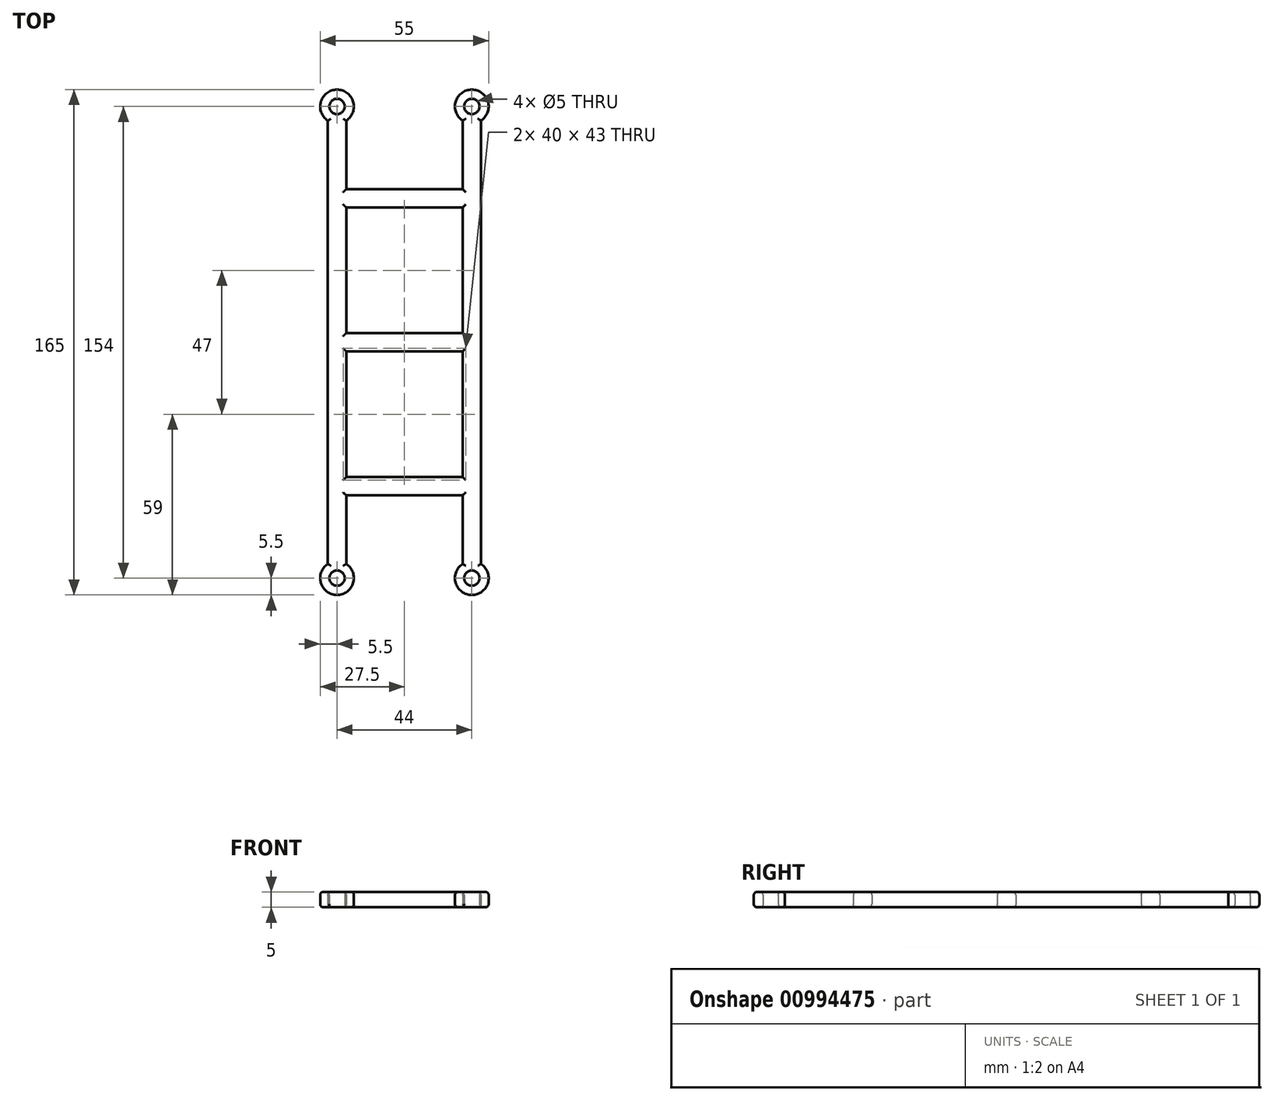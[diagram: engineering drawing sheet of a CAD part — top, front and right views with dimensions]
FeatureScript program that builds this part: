
annotation { "Feature Type Name" : "Feature", "Feature Type Description" : "" }
export const myFeature = defineFeature(function(context is Context, id is Id, definition is map)
    precondition{}
    {
        {
            assignVariable(context, id + "F0", {"name" : "winder_height", "anyValue" : 5});
        }
        {
            var Q0;
            Q0=qCreatedBy(makeId("Top.planeOp"),FACE);
            var sketch = newSketch(context, id + "F1", { "sketchPlane" : qUnion([Q0])});
            skPoint(sketch, "E0.middle", {"position": v(0, 0) * mm});
            skLineSegment(sketch, "E1.bottom", {"start": v(0, 0) * mm, "end": v(25, 0) * mm});
            skLineSegment(sketch, "E1.left", {"start": v(0, 0) * mm, "end": v(0, 50) * mm});
            skLineSegment(sketch, "E1.right", {"start": v(25, 0) * mm, "end": v(25, 50) * mm});
            skLineSegment(sketch, "E2.bottom", {"start": v(25, 50) * mm, "end": v(19, 50) * mm, "construction": true});
            skLineSegment(sketch, "E3", {"start": v(0, 50) * mm, "end": v(19, 50) * mm});
            skLineSegment(sketch, "E4", {"start": v(25, 50) * mm, "end": v(25, 80) * mm});
            skLineSegment(sketch, "E5", {"start": v(25, 80) * mm, "end": v(19, 80) * mm});
            skLineSegment(sketch, "E6", {"start": v(19, 80) * mm, "end": v(19, 50) * mm});
            skLineSegment(sketch, "E7", {"start": v(22, 50) * mm, "end": v(22, 77) * mm, "construction": true});
            skCircle(sketch, "E8", {"center": v(22, 77) * mm, "radius": 2.5 * mm});
            skLineSegment(sketch, "E9.bottom", {"start": v(0, 44) * mm, "end": v(19, 44) * mm});
            skLineSegment(sketch, "E9.top", {"start": v(0, 3) * mm, "end": v(19, 3) * mm});
            skLineSegment(sketch, "E9.left", {"start": v(0, 44) * mm, "end": v(0, 3) * mm});
            skLineSegment(sketch, "E9.right", {"start": v(19, 44) * mm, "end": v(19, 3) * mm});
            skCircle(sketch, "E10", {"center": v(22, 77) * mm, "radius": 5.5 * mm});
            skSolve(sketch);
        }
        {
            var Q0;
            {var subQ8=sQuery(id+"F1.wireOp",EDGE,"E1.bottom");Q0=makeQuery(id+"F1.imprint","IMPRINT",FACE,{"disambiguationData":[TD([[makeQuery(id+"F1.imprint","IMPRINT",EDGE,{"derivedFrom":subQ8}),1.0]])]});}
            var Q1;
            {var subQ0=sQuery(id+"F1.wireOp",EDGE,"E5");Q1=makeQuery(id+"F1.imprint","IMPRINT",FACE,{"disambiguationData":[TD([[makeQuery(id+"F1.imprint","IMPRINT",EDGE,{"derivedFrom":subQ0}),-1.0]])]});}
            var Q2;
            {var subQ1=sQuery(id+"F1.wireOp",EDGE,"E5");Q2=makeQuery(id+"F1.imprint","IMPRINT",FACE,{"disambiguationData":[TD([[makeQuery(id+"F1.imprint","IMPRINT",EDGE,{"derivedFrom":subQ1}),1.0]])]});}
            var Q3;
            Q3=sQuery(id+"F1.wireOp",EDGE,"E2.bottom");
            extrude(context, id + "F2", {"entities" : qUnion([Q0, Q1, Q2]), "surfaceEntities" : qUnion([Q3]), "depth" : (getVariable(context, 'winder_height')) * mm, "offsetDistance" : 25 * mm});
        }
        {
            var Q0;
            Q0=makeQuery(id+"F2.opExtrude","SWEPT_BODY",BODY,{"disambiguationData":[OSD([sQuery(id+"F1.wireOp",EDGE,"E1.bottom"),sQuery(id+"F1.wireOp",EDGE,"E1.left"),sQuery(id+"F1.wireOp",EDGE,"E1.right"),sQuery(id+"F1.wireOp",EDGE,"E3"),sQuery(id+"F1.wireOp",EDGE,"E4"),sQuery(id+"F1.wireOp",EDGE,"E6"),sQuery(id+"F1.wireOp",EDGE,"E8"),sQuery(id+"F1.wireOp",EDGE,"E9.bottom"),sQuery(id+"F1.wireOp",EDGE,"E9.top"),sQuery(id+"F1.wireOp",EDGE,"E9.right"),sQuery(id+"F1.wireOp",EDGE,"E10")])]});
            var Q1;
            Q1=qCreatedBy(makeId("Front.planeOp"),FACE);
            mirror(context, id + "F3", {"operationType" : NewBodyOperationType.ADD, "entities" : qUnion([Q0]), "mirrorPlane" : qUnion([Q1])});
        }
        {
            var Q0;
            Q0=makeQuery(id+"F2.opExtrude","SWEPT_BODY",BODY,{"disambiguationData":[OSD([sQuery(id+"F1.wireOp",EDGE,"E1.bottom"),sQuery(id+"F1.wireOp",EDGE,"E1.left"),sQuery(id+"F1.wireOp",EDGE,"E1.right"),sQuery(id+"F1.wireOp",EDGE,"E3"),sQuery(id+"F1.wireOp",EDGE,"E4"),sQuery(id+"F1.wireOp",EDGE,"E6"),sQuery(id+"F1.wireOp",EDGE,"E8"),sQuery(id+"F1.wireOp",EDGE,"E9.bottom"),sQuery(id+"F1.wireOp",EDGE,"E9.top"),sQuery(id+"F1.wireOp",EDGE,"E9.right"),sQuery(id+"F1.wireOp",EDGE,"E10")])]});
            var Q1;
            Q1=qCreatedBy(makeId("Right.planeOp"),FACE);
            mirror(context, id + "F4", {"operationType" : NewBodyOperationType.ADD, "entities" : qUnion([Q0]), "mirrorPlane" : qUnion([Q1])});
        }
        {
            var Q0;
            {var subQ0=makeQuery(id+"F2.opExtrude","CAP_FACE",FACE,{"disambiguationData":[OSD([sQuery(id+"F1.wireOp",EDGE,"E1.bottom"),sQuery(id+"F1.wireOp",EDGE,"E1.left"),sQuery(id+"F1.wireOp",EDGE,"E1.right"),sQuery(id+"F1.wireOp",EDGE,"E3"),sQuery(id+"F1.wireOp",EDGE,"E4"),sQuery(id+"F1.wireOp",EDGE,"E6"),sQuery(id+"F1.wireOp",EDGE,"E8"),sQuery(id+"F1.wireOp",EDGE,"E9.bottom"),sQuery(id+"F1.wireOp",EDGE,"E9.top"),sQuery(id+"F1.wireOp",EDGE,"E9.right"),sQuery(id+"F1.wireOp",EDGE,"E10")])],"isStart":true});var subQ1=makeQuery(id+"F3.boolean.opBoolean","MERGE",FACE,{"derivedFrom":[subQ0,makeQuery(id+"F3.opPattern","COPY",FACE,{"derivedFrom":subQ0,"instanceName":"1"})]});Q0=makeQuery(id+"F4.boolean.opBoolean","MERGE",FACE,{"derivedFrom":[subQ1,makeQuery(id+"F4.opPattern","COPY",FACE,{"derivedFrom":subQ1,"instanceName":"1"})]});}
            var Q1;
            {var subQ0=makeQuery(id+"F2.opExtrude","CAP_FACE",FACE,{"disambiguationData":[OSD([sQuery(id+"F1.wireOp",EDGE,"E1.bottom"),sQuery(id+"F1.wireOp",EDGE,"E1.left"),sQuery(id+"F1.wireOp",EDGE,"E1.right"),sQuery(id+"F1.wireOp",EDGE,"E3"),sQuery(id+"F1.wireOp",EDGE,"E4"),sQuery(id+"F1.wireOp",EDGE,"E6"),sQuery(id+"F1.wireOp",EDGE,"E8"),sQuery(id+"F1.wireOp",EDGE,"E9.bottom"),sQuery(id+"F1.wireOp",EDGE,"E9.top"),sQuery(id+"F1.wireOp",EDGE,"E9.right"),sQuery(id+"F1.wireOp",EDGE,"E10")])],"isStart":false});var subQ1=makeQuery(id+"F3.boolean.opBoolean","MERGE",FACE,{"derivedFrom":[subQ0,makeQuery(id+"F3.opPattern","COPY",FACE,{"derivedFrom":subQ0,"instanceName":"1"})]});Q1=makeQuery(id+"F4.boolean.opBoolean","MERGE",FACE,{"derivedFrom":[subQ1,makeQuery(id+"F4.opPattern","COPY",FACE,{"derivedFrom":subQ1,"instanceName":"1"})]});}
            fillet(context, id + "F5", {"entities" : qUnion([Q0, Q1]), "radius" : 1 * mm, "tangentPropagation" : true, "allowEdgeOverflow" : false});
        }
    });
